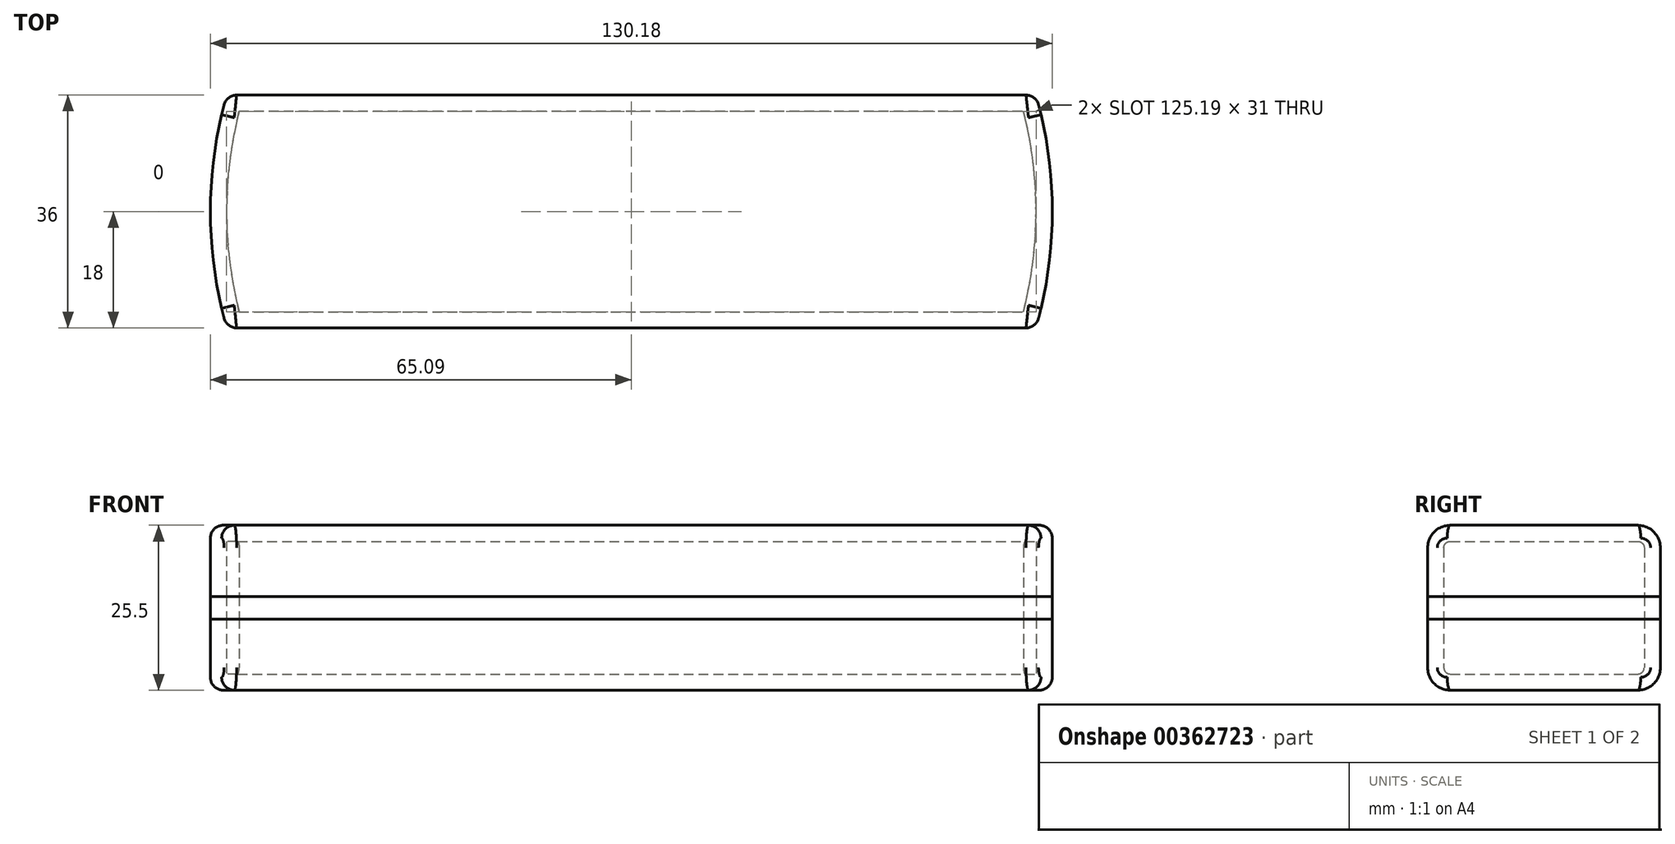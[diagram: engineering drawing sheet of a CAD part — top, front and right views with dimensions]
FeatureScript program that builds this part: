
annotation { "Feature Type Name" : "Feature", "Feature Type Description" : "" }
export const myFeature = defineFeature(function(context is Context, id is Id, definition is map)
    precondition{}
    {
        {
            var Q0;
            Q0=qCreatedBy(makeId("Top.planeOp"),FACE);
            var sketch = newSketch(context, id + "F0", { "sketchPlane" : qUnion([Q0])});
            skLineSegment(sketch, "E0.bottom", {"start": v(-62.55, 18) * mm, "end": v(62.55, 18) * mm});
            skLineSegment(sketch, "E0.top", {"start": v(-62.55, -18) * mm, "end": v(62.55, -18) * mm});
            skPoint(sketch, "E0.middle", {"position": v(0, 0) * mm});
            skArc(sketch, "E1", {"start": v(62.55, -18) * mm, "mid": v(65.1, 0) * mm, "end": v(62.55, 18) * mm});
            skArc(sketch, "E2.MirrorCS", {"start": v(-62.55, -18) * mm, "mid": v(-65.1, 0) * mm, "end": v(-62.55, 18) * mm});
            skSolve(sketch);
        }
        {
            var Q0;
            Q0 = qSketchRegion(id + "F0", true);
            extrude(context, id + "F1", {"entities" : qUnion([Q0]), "depth" : 25.5 * mm});
        }
        {
            var Q0;
            Q0=makeQuery(id+"F1.opExtrude","CAP_EDGE",EDGE,{"disambiguationData":[OSD([sQuery(id+"F0.wireOp",EDGE,"E0.top")])],"isStart":false});
            var Q1;
            Q1=makeQuery(id+"F1.opExtrude","CAP_EDGE",EDGE,{"disambiguationData":[OSD([sQuery(id+"F0.wireOp",EDGE,"E0.top")])],"isStart":true});
            var Q2;
            Q2=makeQuery(id+"F1.opExtrude","CAP_EDGE",EDGE,{"disambiguationData":[OSD([sQuery(id+"F0.wireOp",EDGE,"E0.bottom")])],"isStart":false});
            var Q3;
            Q3=makeQuery(id+"F1.opExtrude","CAP_EDGE",EDGE,{"disambiguationData":[OSD([sQuery(id+"F0.wireOp",EDGE,"E0.bottom")])],"isStart":true});
            fillet(context, id + "F2", {"entities" : qUnion([Q0, Q1, Q2, Q3]), "radius" : 3.5 * mm, "tangentPropagation" : true, "allowEdgeOverflow" : false});
        }
        {
            var Q0;
            Q0=makeQuery(id+"F0.imprint","IMPRINT",FACE,{"disambiguationData":[TD([[makeQuery(id+"F0.imprint","IMPRINT",EDGE,{"derivedFrom":sQuery(id+"F0.wireOp",EDGE,"E0.bottom")}),-1.0]])]});
            extrude(context, id + "F3", {"entities" : qUnion([Q0]), "depth" : 3.5 * mm});
        }
        {
            var Q0;
            Q0=makeQuery(id+"F3.opExtrude","SWEPT_BODY",BODY,{"disambiguationData":[OSD([sQuery(id+"F0.wireOp",EDGE,"E0.bottom"),sQuery(id+"F0.wireOp",EDGE,"E0.top"),sQuery(id+"F0.wireOp",EDGE,"E0.left"),sQuery(id+"F0.wireOp",EDGE,"E0.right")])]});
            transform(context, id + "F4", {"entities" : qUnion([Q0]), "transformType" : TransformType.TRANSLATION_3D, "dx" : 0 * mm, "dy" : 0 * mm, "dz" : -1.75 * mm, "makeCopy" : false});
        }
        {
            var Q0;
            Q0=makeQuery(id+"F1.opExtrude","SWEPT_BODY",BODY,{"disambiguationData":[OSD([sQuery(id+"F0.wireOp",EDGE,"E0.bottom"),sQuery(id+"F0.wireOp",EDGE,"E0.top"),sQuery(id+"F0.wireOp",EDGE,"E0.left"),sQuery(id+"F0.wireOp",EDGE,"E0.right")])]});
            transform(context, id + "F5", {"entities" : qUnion([Q0]), "transformType" : TransformType.TRANSLATION_3D, "dx" : 0 * mm, "dy" : 0 * mm, "dz" : -12.75 * mm, "makeCopy" : false});
        }
        {
            var Q0;
            Q0=makeQuery(id+"F3.opExtrude","SWEPT_BODY",BODY,{"disambiguationData":[OSD([sQuery(id+"F0.wireOp",EDGE,"E0.bottom"),sQuery(id+"F0.wireOp",EDGE,"E0.top"),sQuery(id+"F0.wireOp",EDGE,"E0.left"),sQuery(id+"F0.wireOp",EDGE,"E0.right")])]});
            var Q1;
            Q1=makeQuery(id+"F1.opExtrude","SWEPT_BODY",BODY,{"disambiguationData":[OSD([sQuery(id+"F0.wireOp",EDGE,"E0.bottom"),sQuery(id+"F0.wireOp",EDGE,"E0.top"),sQuery(id+"F0.wireOp",EDGE,"E0.left"),sQuery(id+"F0.wireOp",EDGE,"E0.right")])]});
            booleanBodies(context, id + "F6", {"operationType" : BooleanOperationType.INTERSECTION, "tools" : qUnion([Q0, Q1]), "keepTools" : true});
        }
        {
            var Q0;
            Q0=makeQuery(id+"F3.opExtrude","SWEPT_BODY",BODY,{"disambiguationData":[OSD([sQuery(id+"F0.wireOp",EDGE,"E0.bottom"),sQuery(id+"F0.wireOp",EDGE,"E0.top"),sQuery(id+"F0.wireOp",EDGE,"E0.left"),sQuery(id+"F0.wireOp",EDGE,"E0.right")])]});
            deleteBodies(context, id + "F7", {"entities" : qUnion([Q0])});
        }
        {
            var Q0;
            {var subQ0=sQuery(id+"F0.wireOp",EDGE,"E0.right");var subQ1=sQuery(id+"F0.wireOp",EDGE,"E0.left");var subQ2=sQuery(id+"F0.wireOp",EDGE,"E0.top");var subQ3=sQuery(id+"F0.wireOp",EDGE,"E0.bottom");Q0=makeQuery(id+"F6.opBoolean","INTERSECT",BODY,{"derivedFrom":[makeQuery(id+"F1.opExtrude","SWEPT_BODY",BODY,{"disambiguationData":[OSD([subQ3,subQ2,subQ1,subQ0])]}),makeQuery(id+"F3.opExtrude","SWEPT_BODY",BODY,{"disambiguationData":[OSD([subQ3,subQ2,subQ1,subQ0])]})]});}
            transform(context, id + "F8", {"entities" : qUnion([Q0]), "transformType" : TransformType.TRANSLATION_3D, "dx" : 0 * mm, "dy" : 0 * mm, "dz" : 0 * mm, "makeCopy" : true});
        }
        {
            var Q0;
            {var subQ0=sQuery(id+"F0.wireOp",EDGE,"E0.right");var subQ1=sQuery(id+"F0.wireOp",EDGE,"E0.left");var subQ2=sQuery(id+"F0.wireOp",EDGE,"E0.top");var subQ3=sQuery(id+"F0.wireOp",EDGE,"E0.bottom");Q0=makeQuery(id+"F8.opPattern","COPY",BODY,{"derivedFrom":makeQuery(id+"F6.opBoolean","INTERSECT",BODY,{"derivedFrom":[makeQuery(id+"F1.opExtrude","SWEPT_BODY",BODY,{"disambiguationData":[OSD([subQ3,subQ2,subQ1,subQ0])]}),makeQuery(id+"F3.opExtrude","SWEPT_BODY",BODY,{"disambiguationData":[OSD([subQ3,subQ2,subQ1,subQ0])]})]}),"instanceName":"1"});}
            var Q1;
            Q1=makeQuery(id+"F1.opExtrude","SWEPT_BODY",BODY,{"disambiguationData":[OSD([sQuery(id+"F0.wireOp",EDGE,"E0.bottom"),sQuery(id+"F0.wireOp",EDGE,"E0.top"),sQuery(id+"F0.wireOp",EDGE,"E0.left"),sQuery(id+"F0.wireOp",EDGE,"E0.right")])]});
            booleanBodies(context, id + "F9", {"operationType" : BooleanOperationType.SUBTRACTION, "tools" : qUnion([Q0]), "targets" : qUnion([Q1])});
        }
        {
            var Q0;
            Q0=makeQuery(id+"F1.opExtrude","CAP_EDGE",EDGE,{"disambiguationData":[OSD([sQuery(id+"F0.wireOp",EDGE,"E1")])],"isStart":false});
            var Q1;
            Q1=makeQuery(id+"F2.opFillet","BLEND_EDGE",EDGE,{"blendedFrom":[makeQuery(id+"F1.opExtrude","CAP_EDGE",EDGE,{"disambiguationData":[OSD([sQuery(id+"F0.wireOp",EDGE,"E0.bottom")])],"isStart":false}),makeQuery(id+"F1.opExtrude","SWEPT_FACE",FACE,{"disambiguationData":[OSD([sQuery(id+"F0.wireOp",EDGE,"E1")])]})],"blendedInto":[makeQuery(id+"F1.opExtrude","SWEPT_FACE",FACE,{"disambiguationData":[OSD([sQuery(id+"F0.wireOp",EDGE,"E1")])]})]});
            var Q2;
            {var subQ0=sQuery(id+"F0.wireOp",EDGE,"E0.bottom");var subQ1=sQuery(id+"F0.wireOp",EDGE,"E1");Q2=makeQuery(id+"F9.opBoolean","SPLIT",EDGE,{"disambiguationData":[TD([makeQuery(id+"F2.opFillet","BLEND_FACE",FACE,{"disambiguationData":[OSD([subQ0]),TDD([makeQuery(id+"F1.opExtrude","CAP_EDGE",EDGE,{"disambiguationData":[OSD([subQ0])],"isStart":false})])]})])],"derivedFrom":makeQuery(id+"F1.opExtrude","SWEPT_EDGE",EDGE,{"disambiguationData":[OSD([subQ0,subQ1])]})});}
            var Q3;
            {var subQ0=sQuery(id+"F0.wireOp",EDGE,"E0.bottom");var subQ1=sQuery(id+"F0.wireOp",EDGE,"E1");Q3=makeQuery(id+"F9.opBoolean","SPLIT",EDGE,{"disambiguationData":[TD([makeQuery(id+"F2.opFillet","BLEND_FACE",FACE,{"disambiguationData":[OSD([subQ0]),TDD([makeQuery(id+"F1.opExtrude","CAP_EDGE",EDGE,{"disambiguationData":[OSD([subQ0])],"isStart":true})])]})])],"derivedFrom":makeQuery(id+"F1.opExtrude","SWEPT_EDGE",EDGE,{"disambiguationData":[OSD([subQ0,subQ1])]})});}
            var Q4;
            Q4=makeQuery(id+"F2.opFillet","BLEND_EDGE",EDGE,{"blendedFrom":[makeQuery(id+"F1.opExtrude","CAP_EDGE",EDGE,{"disambiguationData":[OSD([sQuery(id+"F0.wireOp",EDGE,"E0.bottom")])],"isStart":true}),makeQuery(id+"F1.opExtrude","SWEPT_FACE",FACE,{"disambiguationData":[OSD([sQuery(id+"F0.wireOp",EDGE,"E1")])]})],"blendedInto":[makeQuery(id+"F1.opExtrude","SWEPT_FACE",FACE,{"disambiguationData":[OSD([sQuery(id+"F0.wireOp",EDGE,"E1")])]})]});
            var Q5;
            Q5=makeQuery(id+"F6.opBoolean","COPY",EDGE,{"derivedFrom":makeQuery(id+"F3.opExtrude","SWEPT_EDGE",EDGE,{"disambiguationData":[OSD([sQuery(id+"F0.wireOp",EDGE,"E0.bottom"),sQuery(id+"F0.wireOp",EDGE,"E1")])]})});
            var Q6;
            Q6=makeQuery(id+"F6.opBoolean","COPY",EDGE,{"derivedFrom":makeQuery(id+"F3.opExtrude","SWEPT_EDGE",EDGE,{"disambiguationData":[OSD([sQuery(id+"F0.wireOp",EDGE,"E0.top"),sQuery(id+"F0.wireOp",EDGE,"E1")])]})});
            var Q7;
            {var subQ0=sQuery(id+"F0.wireOp",EDGE,"E0.top");var subQ1=sQuery(id+"F0.wireOp",EDGE,"E1");Q7=makeQuery(id+"F9.opBoolean","SPLIT",EDGE,{"disambiguationData":[TD([makeQuery(id+"F2.opFillet","BLEND_FACE",FACE,{"disambiguationData":[OSD([subQ0]),TDD([makeQuery(id+"F1.opExtrude","CAP_EDGE",EDGE,{"disambiguationData":[OSD([subQ0])],"isStart":false})])]})])],"derivedFrom":makeQuery(id+"F1.opExtrude","SWEPT_EDGE",EDGE,{"disambiguationData":[OSD([subQ0,subQ1])]})});}
            var Q8;
            Q8=makeQuery(id+"F2.opFillet","BLEND_EDGE",EDGE,{"blendedFrom":[makeQuery(id+"F1.opExtrude","CAP_EDGE",EDGE,{"disambiguationData":[OSD([sQuery(id+"F0.wireOp",EDGE,"E0.top")])],"isStart":false}),makeQuery(id+"F1.opExtrude","SWEPT_FACE",FACE,{"disambiguationData":[OSD([sQuery(id+"F0.wireOp",EDGE,"E1")])]})],"blendedInto":[makeQuery(id+"F1.opExtrude","SWEPT_FACE",FACE,{"disambiguationData":[OSD([sQuery(id+"F0.wireOp",EDGE,"E1")])]})]});
            var Q9;
            {var subQ0=sQuery(id+"F0.wireOp",EDGE,"E0.top");var subQ1=sQuery(id+"F0.wireOp",EDGE,"E1");Q9=makeQuery(id+"F9.opBoolean","SPLIT",EDGE,{"disambiguationData":[TD([makeQuery(id+"F2.opFillet","BLEND_FACE",FACE,{"disambiguationData":[OSD([subQ0]),TDD([makeQuery(id+"F1.opExtrude","CAP_EDGE",EDGE,{"disambiguationData":[OSD([subQ0])],"isStart":true})])]})])],"derivedFrom":makeQuery(id+"F1.opExtrude","SWEPT_EDGE",EDGE,{"disambiguationData":[OSD([subQ0,subQ1])]})});}
            var Q10;
            Q10=makeQuery(id+"F2.opFillet","BLEND_EDGE",EDGE,{"blendedFrom":[makeQuery(id+"F1.opExtrude","CAP_EDGE",EDGE,{"disambiguationData":[OSD([sQuery(id+"F0.wireOp",EDGE,"E0.top")])],"isStart":true}),makeQuery(id+"F1.opExtrude","SWEPT_FACE",FACE,{"disambiguationData":[OSD([sQuery(id+"F0.wireOp",EDGE,"E1")])]})],"blendedInto":[makeQuery(id+"F1.opExtrude","SWEPT_FACE",FACE,{"disambiguationData":[OSD([sQuery(id+"F0.wireOp",EDGE,"E1")])]})]});
            var Q11;
            Q11=makeQuery(id+"F1.opExtrude","CAP_EDGE",EDGE,{"disambiguationData":[OSD([sQuery(id+"F0.wireOp",EDGE,"E1")])],"isStart":true});
            var Q12;
            {var subQ0=sQuery(id+"F0.wireOp",EDGE,"E0.bottom");var subQ1=sQuery(id+"F0.wireOp",EDGE,"E2.MirrorCS");Q12=makeQuery(id+"F9.opBoolean","SPLIT",EDGE,{"disambiguationData":[TD([makeQuery(id+"F2.opFillet","BLEND_FACE",FACE,{"disambiguationData":[OSD([subQ0]),TDD([makeQuery(id+"F1.opExtrude","CAP_EDGE",EDGE,{"disambiguationData":[OSD([subQ0])],"isStart":false})])]})])],"derivedFrom":makeQuery(id+"F1.opExtrude","SWEPT_EDGE",EDGE,{"disambiguationData":[OSD([subQ0,subQ1])]})});}
            var Q13;
            Q13=makeQuery(id+"F2.opFillet","BLEND_EDGE",EDGE,{"blendedFrom":[makeQuery(id+"F1.opExtrude","CAP_EDGE",EDGE,{"disambiguationData":[OSD([sQuery(id+"F0.wireOp",EDGE,"E0.bottom")])],"isStart":false}),makeQuery(id+"F1.opExtrude","SWEPT_FACE",FACE,{"disambiguationData":[OSD([sQuery(id+"F0.wireOp",EDGE,"E2.MirrorCS")])]})],"blendedInto":[makeQuery(id+"F1.opExtrude","SWEPT_FACE",FACE,{"disambiguationData":[OSD([sQuery(id+"F0.wireOp",EDGE,"E2.MirrorCS")])]})]});
            var Q14;
            Q14=makeQuery(id+"F1.opExtrude","CAP_EDGE",EDGE,{"disambiguationData":[OSD([sQuery(id+"F0.wireOp",EDGE,"E2.MirrorCS")])],"isStart":false});
            var Q15;
            Q15=makeQuery(id+"F6.opBoolean","COPY",EDGE,{"derivedFrom":makeQuery(id+"F3.opExtrude","SWEPT_EDGE",EDGE,{"disambiguationData":[OSD([sQuery(id+"F0.wireOp",EDGE,"E0.bottom"),sQuery(id+"F0.wireOp",EDGE,"E2.MirrorCS")])]})});
            var Q16;
            {var subQ0=sQuery(id+"F0.wireOp",EDGE,"E0.bottom");var subQ1=sQuery(id+"F0.wireOp",EDGE,"E2.MirrorCS");Q16=makeQuery(id+"F9.opBoolean","SPLIT",EDGE,{"disambiguationData":[TD([makeQuery(id+"F2.opFillet","BLEND_FACE",FACE,{"disambiguationData":[OSD([subQ0]),TDD([makeQuery(id+"F1.opExtrude","CAP_EDGE",EDGE,{"disambiguationData":[OSD([subQ0])],"isStart":true})])]})])],"derivedFrom":makeQuery(id+"F1.opExtrude","SWEPT_EDGE",EDGE,{"disambiguationData":[OSD([subQ0,subQ1])]})});}
            var Q17;
            Q17=makeQuery(id+"F1.opExtrude","CAP_EDGE",EDGE,{"disambiguationData":[OSD([sQuery(id+"F0.wireOp",EDGE,"E2.MirrorCS")])],"isStart":true});
            var Q18;
            Q18=makeQuery(id+"F2.opFillet","BLEND_EDGE",EDGE,{"blendedFrom":[makeQuery(id+"F1.opExtrude","CAP_EDGE",EDGE,{"disambiguationData":[OSD([sQuery(id+"F0.wireOp",EDGE,"E0.bottom")])],"isStart":true}),makeQuery(id+"F1.opExtrude","SWEPT_FACE",FACE,{"disambiguationData":[OSD([sQuery(id+"F0.wireOp",EDGE,"E2.MirrorCS")])]})],"blendedInto":[makeQuery(id+"F1.opExtrude","SWEPT_FACE",FACE,{"disambiguationData":[OSD([sQuery(id+"F0.wireOp",EDGE,"E2.MirrorCS")])]})]});
            var Q19;
            Q19=makeQuery(id+"F2.opFillet","BLEND_EDGE",EDGE,{"blendedFrom":[makeQuery(id+"F1.opExtrude","CAP_EDGE",EDGE,{"disambiguationData":[OSD([sQuery(id+"F0.wireOp",EDGE,"E0.top")])],"isStart":true}),makeQuery(id+"F1.opExtrude","SWEPT_FACE",FACE,{"disambiguationData":[OSD([sQuery(id+"F0.wireOp",EDGE,"E2.MirrorCS")])]})],"blendedInto":[makeQuery(id+"F1.opExtrude","SWEPT_FACE",FACE,{"disambiguationData":[OSD([sQuery(id+"F0.wireOp",EDGE,"E2.MirrorCS")])]})]});
            var Q20;
            {var subQ0=sQuery(id+"F0.wireOp",EDGE,"E0.top");var subQ1=sQuery(id+"F0.wireOp",EDGE,"E2.MirrorCS");Q20=makeQuery(id+"F9.opBoolean","SPLIT",EDGE,{"disambiguationData":[TD([makeQuery(id+"F2.opFillet","BLEND_FACE",FACE,{"disambiguationData":[OSD([subQ0]),TDD([makeQuery(id+"F1.opExtrude","CAP_EDGE",EDGE,{"disambiguationData":[OSD([subQ0])],"isStart":true})])]})])],"derivedFrom":makeQuery(id+"F1.opExtrude","SWEPT_EDGE",EDGE,{"disambiguationData":[OSD([subQ0,subQ1])]})});}
            var Q21;
            Q21=makeQuery(id+"F6.opBoolean","COPY",EDGE,{"derivedFrom":makeQuery(id+"F3.opExtrude","SWEPT_EDGE",EDGE,{"disambiguationData":[OSD([sQuery(id+"F0.wireOp",EDGE,"E0.top"),sQuery(id+"F0.wireOp",EDGE,"E2.MirrorCS")])]})});
            var Q22;
            {var subQ0=sQuery(id+"F0.wireOp",EDGE,"E0.top");var subQ1=sQuery(id+"F0.wireOp",EDGE,"E2.MirrorCS");Q22=makeQuery(id+"F9.opBoolean","SPLIT",EDGE,{"disambiguationData":[TD([makeQuery(id+"F2.opFillet","BLEND_FACE",FACE,{"disambiguationData":[OSD([subQ0]),TDD([makeQuery(id+"F1.opExtrude","CAP_EDGE",EDGE,{"disambiguationData":[OSD([subQ0])],"isStart":false})])]})])],"derivedFrom":makeQuery(id+"F1.opExtrude","SWEPT_EDGE",EDGE,{"disambiguationData":[OSD([subQ0,subQ1])]})});}
            var Q23;
            Q23=makeQuery(id+"F2.opFillet","BLEND_EDGE",EDGE,{"blendedFrom":[makeQuery(id+"F1.opExtrude","CAP_EDGE",EDGE,{"disambiguationData":[OSD([sQuery(id+"F0.wireOp",EDGE,"E0.top")])],"isStart":false}),makeQuery(id+"F1.opExtrude","SWEPT_FACE",FACE,{"disambiguationData":[OSD([sQuery(id+"F0.wireOp",EDGE,"E2.MirrorCS")])]})],"blendedInto":[makeQuery(id+"F1.opExtrude","SWEPT_FACE",FACE,{"disambiguationData":[OSD([sQuery(id+"F0.wireOp",EDGE,"E2.MirrorCS")])]})]});
            fillet(context, id + "F10", {"entities" : qUnion([Q0, Q1, Q2, Q3, Q4, Q5, Q6, Q7, Q8, Q9, Q10, Q11, Q12, Q13, Q14, Q15, Q16, Q17, Q18, Q19, Q20, Q21, Q22, Q23]), "radius" : 2 * mm, "tangentPropagation" : true, "allowEdgeOverflow" : false});
        }
        {
            var Q0;
            Q0=makeQuery(id+"F9.opBoolean","COPY",FACE,{"derivedFrom":makeQuery(id+"F8.opPattern","COPY",FACE,{"derivedFrom":makeQuery(id+"F6.opBoolean","COPY",FACE,{"derivedFrom":makeQuery(id+"F3.opExtrude","CAP_FACE",FACE,{"disambiguationData":[OSD([sQuery(id+"F0.wireOp",EDGE,"E0.bottom"),sQuery(id+"F0.wireOp",EDGE,"E0.top"),sQuery(id+"F0.wireOp",EDGE,"E1"),sQuery(id+"F0.wireOp",EDGE,"E2.MirrorCS")])],"isStart":true})}),"instanceName":"1"})});
            var Q1;
            Q1=makeQuery(id+"F9.opBoolean","COPY",FACE,{"derivedFrom":makeQuery(id+"F8.opPattern","COPY",FACE,{"derivedFrom":makeQuery(id+"F6.opBoolean","COPY",FACE,{"derivedFrom":makeQuery(id+"F3.opExtrude","CAP_FACE",FACE,{"disambiguationData":[OSD([sQuery(id+"F0.wireOp",EDGE,"E0.bottom"),sQuery(id+"F0.wireOp",EDGE,"E0.top"),sQuery(id+"F0.wireOp",EDGE,"E1"),sQuery(id+"F0.wireOp",EDGE,"E2.MirrorCS")])],"isStart":false})}),"instanceName":"1"})});
            var Q2;
            Q2=makeQuery(id+"F9.opBoolean","SPLIT",BODY,{"disambiguationData":[OD(0.0)],"derivedFrom":makeQuery(id+"F1.opExtrude","SWEPT_BODY",BODY,{"disambiguationData":[OSD([sQuery(id+"F0.wireOp",EDGE,"E0.bottom"),sQuery(id+"F0.wireOp",EDGE,"E0.top"),sQuery(id+"F0.wireOp",EDGE,"E1"),sQuery(id+"F0.wireOp",EDGE,"E2.MirrorCS")])]})});
            var Q3;
            {var subQ0=sQuery(id+"F0.wireOp",EDGE,"E2.MirrorCS");var subQ1=sQuery(id+"F0.wireOp",EDGE,"E1");var subQ2=sQuery(id+"F0.wireOp",EDGE,"E0.top");var subQ3=sQuery(id+"F0.wireOp",EDGE,"E0.bottom");Q3=makeQuery(id+"F6.opBoolean","INTERSECT",BODY,{"derivedFrom":[makeQuery(id+"F1.opExtrude","SWEPT_BODY",BODY,{"disambiguationData":[OSD([subQ3,subQ2,subQ1,subQ0])]}),makeQuery(id+"F3.opExtrude","SWEPT_BODY",BODY,{"disambiguationData":[OSD([subQ3,subQ2,subQ1,subQ0])]})]});}
            var Q4;
            Q4=makeQuery(id+"F9.opBoolean","SPLIT",BODY,{"disambiguationData":[OD(1.0)],"derivedFrom":makeQuery(id+"F1.opExtrude","SWEPT_BODY",BODY,{"disambiguationData":[OSD([sQuery(id+"F0.wireOp",EDGE,"E0.bottom"),sQuery(id+"F0.wireOp",EDGE,"E0.top"),sQuery(id+"F0.wireOp",EDGE,"E1"),sQuery(id+"F0.wireOp",EDGE,"E2.MirrorCS")])]})});
            shell(context, id + "F11", {"entities" : qUnion([Q0, Q1]), "parts" : qUnion([Q2, Q3, Q4]), "thickness" : 2.5 * mm});
        }
        {
            var Q0;
            Q0=makeQuery(id+"F6.opBoolean","COPY",FACE,{"derivedFrom":makeQuery(id+"F3.opExtrude","CAP_FACE",FACE,{"disambiguationData":[OSD([sQuery(id+"F0.wireOp",EDGE,"E0.bottom"),sQuery(id+"F0.wireOp",EDGE,"E0.top"),sQuery(id+"F0.wireOp",EDGE,"E1"),sQuery(id+"F0.wireOp",EDGE,"E2.MirrorCS")])],"isStart":true})});
            var Q1;
            Q1=makeQuery(id+"F6.opBoolean","COPY",FACE,{"derivedFrom":makeQuery(id+"F3.opExtrude","CAP_FACE",FACE,{"disambiguationData":[OSD([sQuery(id+"F0.wireOp",EDGE,"E0.bottom"),sQuery(id+"F0.wireOp",EDGE,"E0.top"),sQuery(id+"F0.wireOp",EDGE,"E1"),sQuery(id+"F0.wireOp",EDGE,"E2.MirrorCS")])],"isStart":false})});
            shell(context, id + "F12", {"entities" : qUnion([Q0, Q1]), "thickness" : 2.5 * mm});
        }
    });
